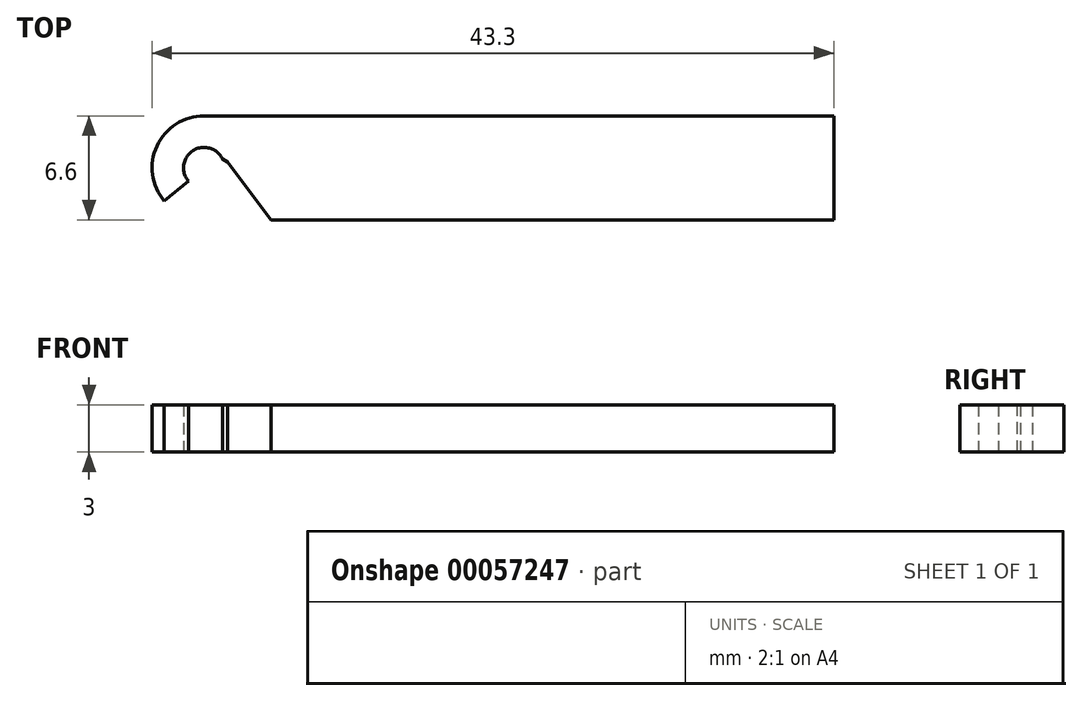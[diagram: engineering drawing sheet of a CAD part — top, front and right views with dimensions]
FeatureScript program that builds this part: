
annotation { "Feature Type Name" : "Feature", "Feature Type Description" : "" }
export const myFeature = defineFeature(function(context is Context, id is Id, definition is map)
    precondition{}
    {
        {
            var Q0;
            Q0=qCreatedBy(makeId("Top.planeOp"),FACE);
            var sketch = newSketch(context, id + "F0", { "sketchPlane" : qUnion([Q0])});
            skLineSegment(sketch, "E0", {"start": v(-40, 0) * mm, "end": v(40, 0) * mm, "construction": true});
            skCircle(sketch, "E1", {"center": v(-40, 0) * mm, "radius": 1.3 * mm});
            skArc(sketch, "E2.0", {"start": v(-40, 3.3) * mm, "mid": v(-42.33, -2.33) * mm, "end": v(-36.7, 0) * mm});
            skLineSegment(sketch, "E3", {"start": v(-40, 0) * mm, "end": v(-41, -0.84) * mm, "construction": true});
            skLineSegment(sketch, "E4", {"start": v(-41, -0.84) * mm, "end": v(-42.53, -2.12) * mm});
            skLineSegment(sketch, "E5", {"start": v(-40, 3.3) * mm, "end": v(0, 3.3) * mm});
            skLineSegment(sketch, "E6", {"start": v(0, 0) * mm, "end": v(0, 3.3) * mm});
            skPoint(sketch, "E6.endSnap0", {"position": v(0, 0) * mm});
            skLineSegment(sketch, "E7", {"start": v(-36.7, 0) * mm, "end": v(-38.7, 0) * mm});
            skLineSegment(sketch, "E8", {"start": v(0, -3.3) * mm, "end": v(-35.75, -3.3) * mm});
            skLineSegment(sketch, "E9", {"start": v(0, 0) * mm, "end": v(0, -3.3) * mm});
            skLineSegment(sketch, "E10", {"start": v(-35.75, -3.3) * mm, "end": v(-38.23, 0) * mm});
            skSolve(sketch);
        }
        {
            var Q0;
            {var subQ1=sQuery(id+"F0.wireOp",EDGE,"E4");Q0=makeQuery(id+"F0.imprint","IMPRINT",FACE,{"disambiguationData":[TD([[makeQuery(id+"F0.imprint","IMPRINT",EDGE,{"derivedFrom":subQ1}),-1.0]])]});}
            var Q1;
            {var subQ0=sQuery(id+"F0.wireOp",EDGE,"E7");Q1=makeQuery(id+"F0.imprint","IMPRINT",FACE,{"disambiguationData":[TD([[makeQuery(id+"F0.imprint","IMPRINT",EDGE,{"derivedFrom":subQ0}),1.0]])]});}
            extrude(context, id + "F1", {"entities" : qUnion([Q0, Q1]), "depth" : 3 * mm});
        }
        {
            var Q0;
            Q0=makeQuery(id+"F1.opExtrude","SWEPT_EDGE",EDGE,{"disambiguationData":[OSD([sQuery(id+"F0.wireOp",EDGE,"E1"),sQuery(id+"F0.wireOp",EDGE,"E7")])]});
            chamfer(context, id + "F2", {"entities" : qUnion([Q0]), "width" : 1 * mm, "tangentPropagation" : true});
        }
    });
